# Revit family: Burko F-3900 Triplex
name_source: partatom
category: HLS-Bauteile
units: mm (PartAtom-declared; Revit-internal decimal feet)

## family parameters
Arbeitsebenenbasiert = Nein
Beim Laden mit Abzugskörper schneiden = Nein
Bemaßung runder Anschluss = Durchmesser verwenden
Beschriftungsausrichtung beibehalten = Nein
Gemeinsam genutzt = Nein
Immer vertikal = Ja
Klassifizierung = Keine
Raumberechnungspunkt = Nein
Teiletyp = Normal

## types (4) — shared parameters
Anschluss 2" = 50 mm  [stored 0.164042 ft]
Anschluss 3" = 80 mm  [stored 0.262467 ft]
Datenblatt = https://www.burkhalter-h2o.ch
Homepage = https://www.burkhalter-h2o.ch
LUT = LUT_Burko_F-3900
Steuerung_Tiefe = 75 mm  [stored 0.246063 ft]
zero-valued in all types: Vorgabe-Ansicht

## per-type parameters (varying)
| type | A | B | Behälterkopf | C | F | Harzinhalt_pro_Harzdruckbehälter | Sockel_Absatz_Oben | Sockel_Absatz_Unten | Sockel_Höhe | Steuerung_Breite | Steuerung_Höhe |
| Burko F-3900 - 300L | 770 mm  [stored 2.52625 ft] | 2500 mm  [stored 8.2021 ft] | 200 mm  [stored 0.656168 ft] | 2190 mm  [stored 7.18504 ft] | 1145 mm  [stored 3.75656 ft] | 300L | 365 mm  [stored 1.19751 ft] | 395 mm  [stored 1.29593 ft] | 150 mm  [stored 0.492126 ft] | 250 mm  [stored 0.82021 ft] | 400 mm  [stored 1.31234 ft] |
| Burko F-3900 - 400L | 770 mm  [stored 2.52625 ft] | 2500 mm  [stored 8.2021 ft] | 200 mm  [stored 0.656168 ft] | 2190 mm  [stored 7.18504 ft] | 1145 mm  [stored 3.75656 ft] | 400L | 365 mm  [stored 1.19751 ft] | 395 mm  [stored 1.29593 ft] | 150 mm  [stored 0.492126 ft] | 250 mm  [stored 0.82021 ft] | 400 mm  [stored 1.31234 ft] |
| Burko F-3900 - 600L | 927 mm  [stored 3.04134 ft] | 2570 mm  [stored 8.43176 ft] | 250 mm  [stored 0.82021 ft] | 2260 mm  [stored 7.4147 ft] | 1295 mm  [stored 4.24869 ft] | 600L | 444 mm | 474 mm | 200 mm  [stored 0.656168 ft] | 300 mm  [stored 0.984252 ft] | 450 mm  [stored 1.47638 ft] |
| Burko F-3900 - 1000L | 1226 mm  [stored 4.02231 ft] | 2850 mm  [stored 9.35039 ft] | 400 mm  [stored 1.31234 ft] | 2530 mm  [stored 8.30052 ft] | 1650 mm  [stored 5.41339 ft] | 1000L | 593 mm | 623 mm  [stored 2.04396 ft] | 250 mm  [stored 0.82021 ft] | 300 mm  [stored 0.984252 ft] | 450 mm  [stored 1.47638 ft] |

note: [stored X ft] marks values corroborated as IEEE doubles in the binary element streams (Revit-internal decimal feet)
